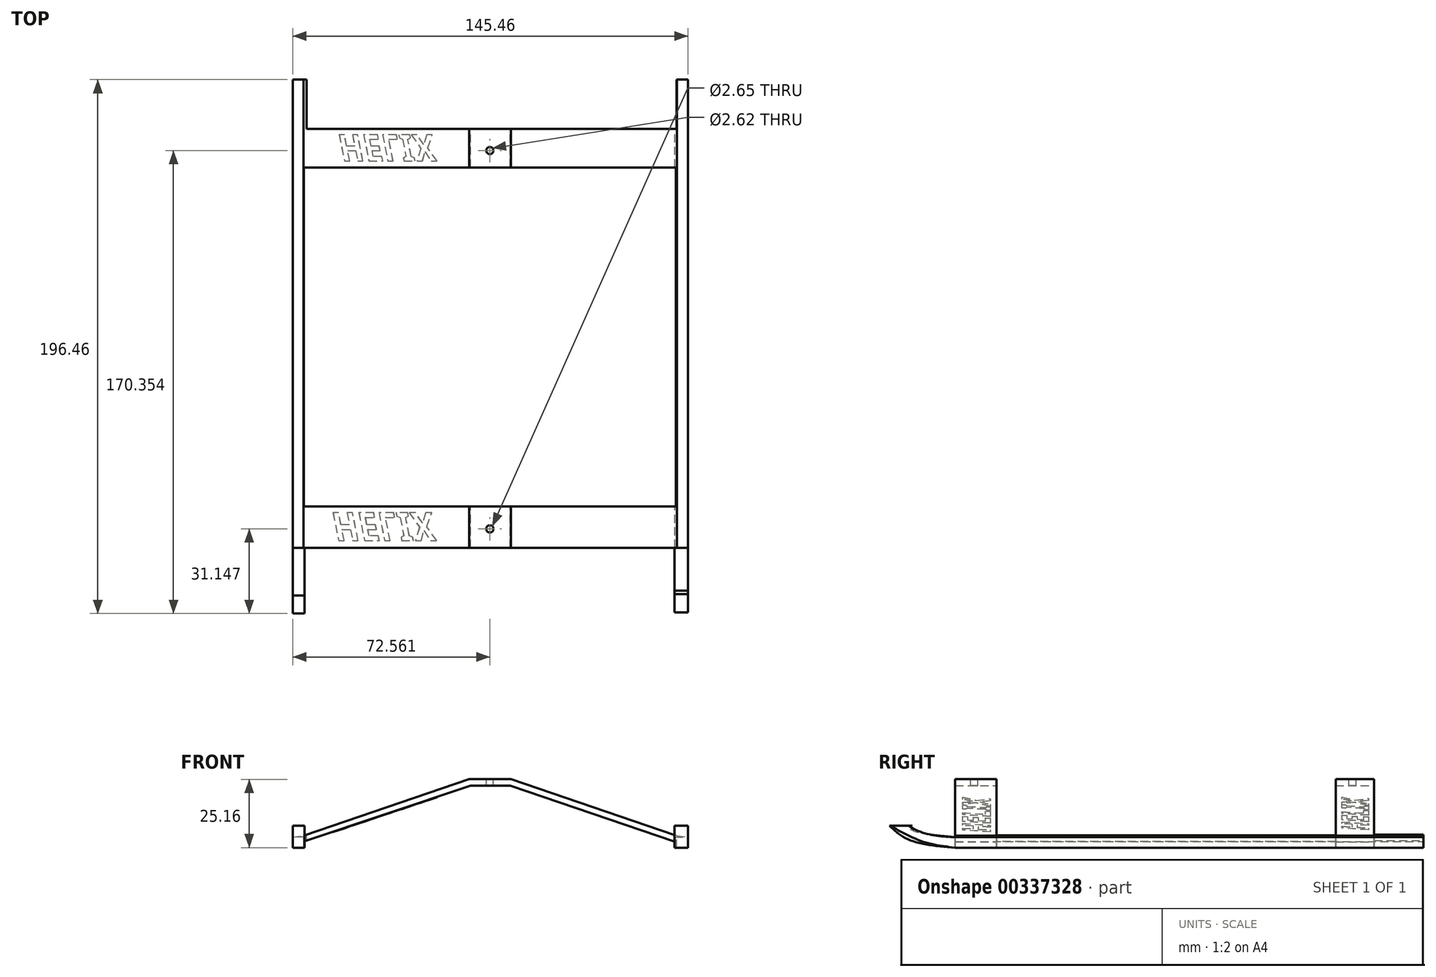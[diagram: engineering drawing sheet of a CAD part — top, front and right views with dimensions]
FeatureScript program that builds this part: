
annotation { "Feature Type Name" : "Feature", "Feature Type Description" : "" }
export const myFeature = defineFeature(function(context is Context, id is Id, definition is map)
    precondition{}
    {
        {
            var Q0;
            Q0=qCreatedBy(makeId("Front.planeOp"),FACE);
            var sketch = newSketch(context, id + "F0", { "sketchPlane" : qUnion([Q0])});
            skLineSegment(sketch, "E0", {"start": v(0, 3.84) * mm, "end": v(62.75, 25.16) * mm});
            skLineSegment(sketch, "E1", {"start": v(140.68, 3.84) * mm, "end": v(78.14, 25.16) * mm});
            skLineSegment(sketch, "E2", {"start": v(78.14, 25.16) * mm, "end": v(62.75, 25.16) * mm});
            skLineSegment(sketch, "E3", {"start": v(0, 3.84) * mm, "end": v(1.8, 4.45) * mm});
            skLineSegment(sketch, "E4", {"start": v(1.8, 4.45) * mm, "end": v(1.8, 0) * mm});
            skLineSegment(sketch, "E5", {"start": v(1.8, 0) * mm, "end": v(-2.22, 0) * mm});
            skLineSegment(sketch, "E6", {"start": v(-2.22, 0) * mm, "end": v(-2.22, 3.84) * mm});
            skLineSegment(sketch, "E7", {"start": v(-2.22, 3.84) * mm, "end": v(1.8, 4.45) * mm});
            skLineSegment(sketch, "E8", {"start": v(140.68, 0) * mm, "end": v(138.42, 0) * mm});
            skLineSegment(sketch, "E9", {"start": v(138.42, 0) * mm, "end": v(138.42, 4.45) * mm});
            skLineSegment(sketch, "E10", {"start": v(138.42, 4.45) * mm, "end": v(143.24, 3.84) * mm});
            skLineSegment(sketch, "E11", {"start": v(143.24, 3.84) * mm, "end": v(143.24, 0) * mm});
            skLineSegment(sketch, "E12", {"start": v(143.24, 0) * mm, "end": v(140.68, 0) * mm});
            skLineSegment(sketch, "E13", {"start": v(0, 3.84) * mm, "end": v(0.55, 2.23) * mm});
            skPoint(sketch, "E13.endSnap0", {"position": v(1.8, 2.23) * mm});
            skLineSegment(sketch, "E14", {"start": v(0.55, 2.23) * mm, "end": v(1.8, 0) * mm});
            skLineSegment(sketch, "E15", {"start": v(1.8, 2.23) * mm, "end": v(63.24, 22.81) * mm});
            skLineSegment(sketch, "E16", {"start": v(63.24, 22.81) * mm, "end": v(77.88, 22.81) * mm});
            skLineSegment(sketch, "E17", {"start": v(77.88, 22.81) * mm, "end": v(138.42, 2.17) * mm});
            skSolve(sketch);
        }
        {
            var Q0;
            Q0 = qSketchRegion(id + "F0", true);
            extrude(context, id + "F1", {"entities" : qUnion([Q0]), "depth" : 172.3 * mm});
        }
        {
            var Q0;
            Q0=makeQuery(id+"F1.opExtrude","SWEPT_FACE",FACE,{"disambiguationData":[OSD([sQuery(id+"F0.wireOp",EDGE,"E2")])]});
            var sketch = newSketch(context, id + "F2", { "sketchPlane" : qUnion([Q0])});
            skLineSegment(sketch, "E18.bottom", {"start": v(139.05, -18.17) * mm, "end": v(2.88, -18.17) * mm});
            skLineSegment(sketch, "E18.top", {"start": v(139.05, 0) * mm, "end": v(2.88, 0) * mm});
            skLineSegment(sketch, "E18.left", {"start": v(139.05, -18.17) * mm, "end": v(139.05, 0) * mm});
            skLineSegment(sketch, "E18.right", {"start": v(2.88, -18.17) * mm, "end": v(2.88, 0) * mm});
            skSolve(sketch);
        }
        {
            var Q0;
            Q0 = qSketchRegion(id + "F2", true);
            extrude(context, id + "F3", {"entities" : qUnion([Q0]), "operationType" : NewBodyOperationType.REMOVE, "oppositeDirection" : true, "depth" : 46 * mm});
        }
        {
            var Q0;
            Q0=makeQuery(id+"F1.opExtrude","SWEPT_FACE",FACE,{"disambiguationData":[OSD([sQuery(id+"F0.wireOp",EDGE,"E2")])]});
            var sketch = newSketch(context, id + "F4", { "sketchPlane" : qUnion([Q0])});
            skLineSegment(sketch, "E19", {"start": v(70.44, -23.63) * mm, "end": v(70.44, -162.76) * mm});
            skPoint(sketch, "E19.startSnap0", {"position": v(70.44, -18.17) * mm});
            skLineSegment(sketch, "E20.bottom", {"start": v(138.8, -32.3) * mm, "end": v(1.92, -32.3) * mm});
            skLineSegment(sketch, "E20.top", {"start": v(138.8, -157.12) * mm, "end": v(1.92, -157.12) * mm});
            skLineSegment(sketch, "E20.left", {"start": v(138.8, -32.3) * mm, "end": v(138.8, -157.12) * mm});
            skLineSegment(sketch, "E20.right", {"start": v(1.92, -32.3) * mm, "end": v(1.92, -157.12) * mm});
            skSolve(sketch);
        }
        {
            var Q0;
            Q0 = qSketchRegion(id + "F4", true);
            extrude(context, id + "F5", {"entities" : qUnion([Q0]), "operationType" : NewBodyOperationType.REMOVE, "oppositeDirection" : true, "depth" : 71.4 * mm});
        }
        {
            var Q0;
            Q0=makeQuery(id+"F1.opExtrude","SWEPT_FACE",FACE,{"disambiguationData":[OSD([sQuery(id+"F0.wireOp",EDGE,"E6")])]});
            var sketch = newSketch(context, id + "F6", { "sketchPlane" : qUnion([Q0])});
            skFitSpline(sketch, "E21", {"points": [v(172.3, 0) * mm, v(189.11, 2.8) * mm, v(196.46, 8.04) * mm], "startDerivative": vector(32.4, 2.62) * mm, "endDerivative": vector(14.99, 14.06) * mm});
            skFitSpline(sketch, "E22", {"points": [v(172.3, 3.84) * mm, v(188.07, 6.3) * mm, v(189.81, 8.04) * mm], "startDerivative": vector(27.63, 2.42) * mm, "endDerivative": vector(3.96, 6.58) * mm});
            skLineSegment(sketch, "E23", {"start": v(189.81, 8.04) * mm, "end": v(196.46, 8.04) * mm});
            skLineSegment(sketch, "E24", {"start": v(172.3, 3.84) * mm, "end": v(172.3, 0) * mm});
            skSolve(sketch);
        }
        {
            var Q0;
            Q0 = qSketchRegion(id + "F6", true);
            extrude(context, id + "F7", {"entities" : qUnion([Q0]), "operationType" : NewBodyOperationType.ADD, "oppositeDirection" : true, "depth" : 4.3 * mm});
        }
        {
            var Q0;
            Q0=makeQuery(id+"F1.opExtrude","SWEPT_FACE",FACE,{"disambiguationData":[OSD([sQuery(id+"F0.wireOp",EDGE,"E11")])]});
            var sketch = newSketch(context, id + "F8", { "sketchPlane" : qUnion([Q0])});
            skFitSpline(sketch, "E25", {"points": [v(-172.3, 0) * mm, v(-184.4, 2.27) * mm, v(-196.1, 8.04) * mm], "startDerivative": vector(-24.91, 2.94) * mm, "endDerivative": vector(-22.71, 13.08) * mm});
            skFitSpline(sketch, "E26", {"points": [v(-172.3, 3.84) * mm, v(-183.87, 5.42) * mm, v(-189.29, 8.04) * mm, v(-188.07, 8.04) * mm], "startDerivative": vector(-23.7, 1.08) * mm, "endDerivative": vector(11.3, -1.4) * mm});
            skLineSegment(sketch, "E27", {"start": v(-196.1, 8.04) * mm, "end": v(-188.07, 8.04) * mm});
            skLineSegment(sketch, "E28", {"start": v(-172.3, 0) * mm, "end": v(-172.3, 3.84) * mm});
            skSolve(sketch);
        }
        {
            var Q0;
            Q0 = qSketchRegion(id + "F8", true);
            extrude(context, id + "F9", {"entities" : qUnion([Q0]), "operationType" : NewBodyOperationType.ADD, "oppositeDirection" : true, "depth" : 4.9 * mm});
        }
        {
            var Q0;
            {var subQ1=sQuery(id+"F0.wireOp",EDGE,"E2");Q0=makeQuery(id+"F5.boolean.opBoolean","SPLIT",FACE,{"disambiguationData":[TD([makeQuery(id+"F5.opExtrude","SWEPT_FACE",FACE,{"disambiguationData":[OSD([sQuery(id+"F4.wireOp",EDGE,"E20.top")])]})])],"derivedFrom":makeQuery(id+"F1.opExtrude","SWEPT_FACE",FACE,{"disambiguationData":[OSD([subQ1])]})});}
            var sketch = newSketch(context, id + "F10", { "sketchPlane" : qUnion([Q0])});
            skLineSegment(sketch, "E29.bottom", {"start": v(78.14, -172.3) * mm, "end": v(62.75, -172.3) * mm});
            skLineSegment(sketch, "E29.top", {"start": v(78.14, -157.12) * mm, "end": v(62.75, -157.12) * mm});
            skLineSegment(sketch, "E29.left", {"start": v(78.14, -172.3) * mm, "end": v(78.14, -157.12) * mm});
            skLineSegment(sketch, "E29.right", {"start": v(62.75, -172.3) * mm, "end": v(62.75, -157.12) * mm});
            skSolve(sketch);
        }
        {
            var Q0;
            Q0=makeQuery(id+"F10.imprint","IMPRINT",FACE,{"disambiguationData":[TD([[makeQuery(id+"F10.imprint","IMPRINT",EDGE,{"derivedFrom":sQuery(id+"F10.wireOp",EDGE,"E29.bottom")}),-1.0]])]});
            var sketch = newSketch(context, id + "F11", { "sketchPlane" : qUnion([Q0])});
            skCircle(sketch, "E30", {"center": v(70.34, -165.31) * mm, "radius": 1.32 * mm});
            skCircle(sketch, "E31", {"center": v(70.34, -26.1) * mm, "radius": 1.31 * mm});
            skSolve(sketch);
        }
        {
            var Q0;
            Q0 = qSketchRegion(id + "F11", true);
            extrude(context, id + "F12", {"entities" : qUnion([Q0]), "operationType" : NewBodyOperationType.REMOVE, "oppositeDirection" : true, "depth" : 25 * mm});
        }
        {
            var Q0;
            Q0=makeQuery(id+"F1.opExtrude","SWEPT_FACE",FACE,{"disambiguationData":[OSD([sQuery(id+"F0.wireOp",EDGE,"E15")])]});
            var sketch = newSketch(context, id + "F13", { "sketchPlane" : qUnion([Q0])});
            skText(sketch, "E32", { "text": "HELIX", "fontName": "NotoSans-BoldItalic.ttf"});
            skText(sketch, "E33", { "text": "HELIX", "fontName": "NotoSans-BoldItalic.ttf"});
            const initialGuessF13  = {"E32": [0.01344, 0.15937, 1, 0, 0.01034], "E33": [0.01586, 0.02028, 1, 0, 0.00976]};
            skSetInitialGuess(sketch, initialGuessF13);
            skSolve(sketch);
        }
        {
            var Q0;
            Q0 = qSketchRegion(id + "F13", true);
            extrude(context, id + "F14", {"entities" : qUnion([Q0]), "operationType" : NewBodyOperationType.ADD, "depth" : 0.1 * mm});
        }
    });
